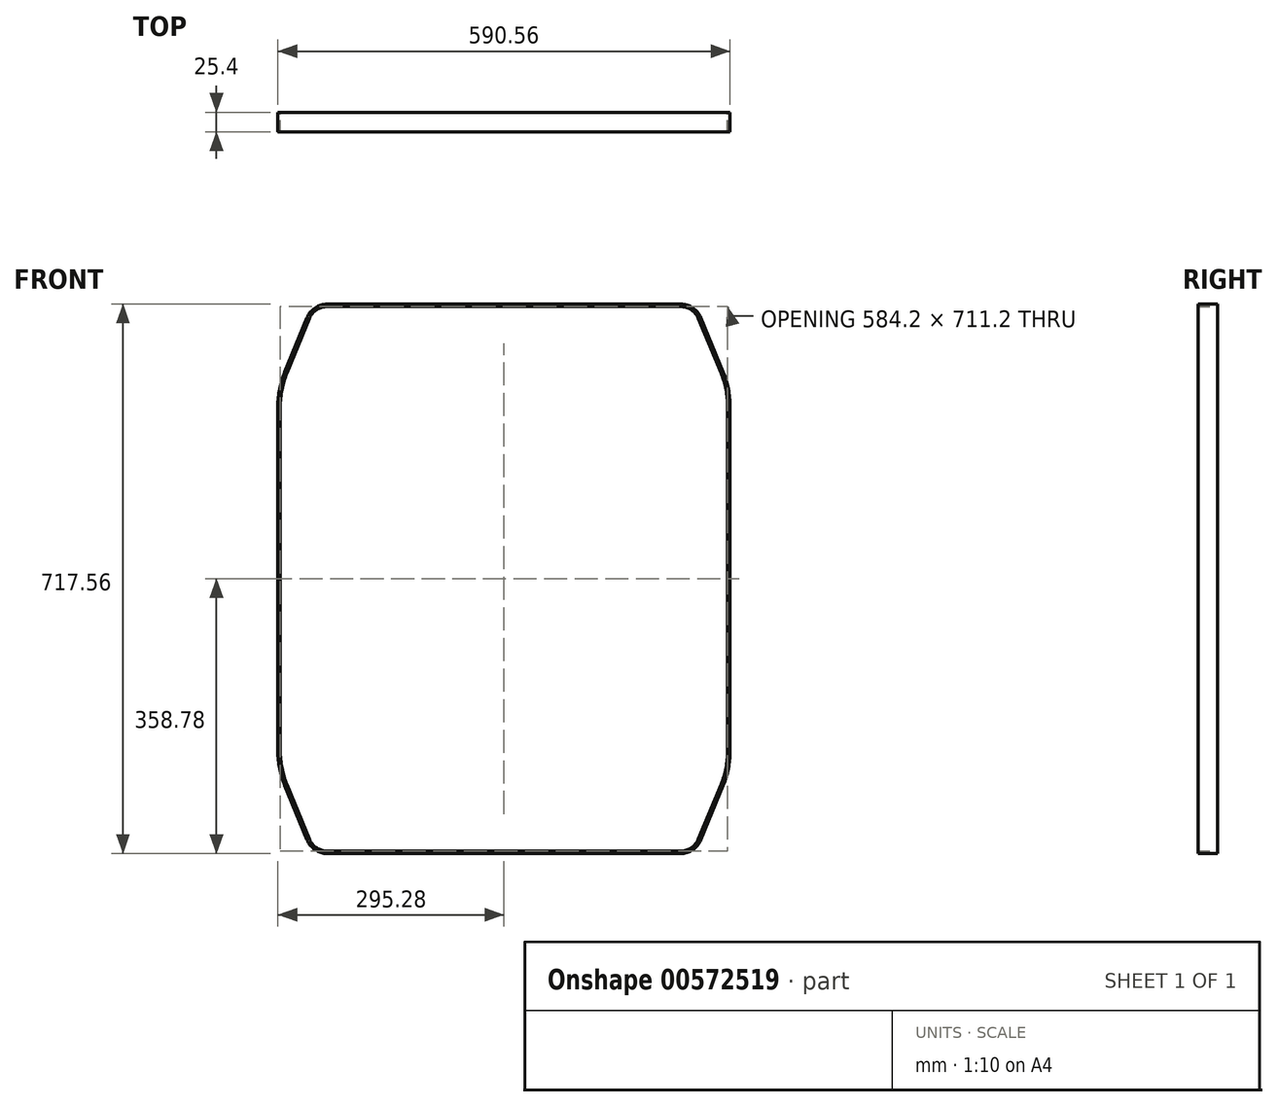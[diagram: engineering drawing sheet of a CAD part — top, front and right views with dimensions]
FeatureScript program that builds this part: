
annotation { "Feature Type Name" : "Feature", "Feature Type Description" : "" }
export const myFeature = defineFeature(function(context is Context, id is Id, definition is map)
    precondition{}
    {
        {
            var Q0;
            Q0=qCreatedBy(makeId("Front.planeOp"),FACE);
            var sketch = newSketch(context, id + "F0", { "sketchPlane" : qUnion([Q0])});
            skPoint(sketch, "E0", {"position": v(0, 0) * mm});
            skPoint(sketch, "E1", {"position": v(0, 711.2) * mm});
            skPoint(sketch, "E2", {"position": v(-584.2, 711.2) * mm});
            skPoint(sketch, "E3", {"position": v(-584.2, 0) * mm});
            skLineSegment(sketch, "E4", {"start": v(-514.35, 711.2) * mm, "end": v(-69.85, 711.2) * mm});
            skLineSegment(sketch, "E5", {"start": v(0, 577.85) * mm, "end": v(0, 133.35) * mm});
            skLineSegment(sketch, "E6", {"start": v(-69.85, 0) * mm, "end": v(-514.35, 0) * mm});
            skLineSegment(sketch, "E7", {"start": v(-584.2, 133.35) * mm, "end": v(-584.2, 577.85) * mm});
            skLineSegment(sketch, "E8", {"start": v(-514.35, 711.2) * mm, "end": v(-522.74, 711.2) * mm});
            skLineSegment(sketch, "E9", {"start": v(-546.23, 695.47) * mm, "end": v(-575.6, 624.16) * mm});
            skLineSegment(sketch, "E10", {"start": v(-584.2, 580.64) * mm, "end": v(-584.2, 577.85) * mm});
            skLineSegment(sketch, "E11", {"start": v(-69.85, 711.2) * mm, "end": v(-61.46, 711.2) * mm});
            skLineSegment(sketch, "E12", {"start": v(-37.97, 695.47) * mm, "end": v(-8.6, 624.16) * mm});
            skLineSegment(sketch, "E13", {"start": v(0, 580.64) * mm, "end": v(0, 577.85) * mm});
            skLineSegment(sketch, "E14", {"start": v(-514.35, 0) * mm, "end": v(-522.74, 0) * mm});
            skLineSegment(sketch, "E15", {"start": v(-546.23, 15.73) * mm, "end": v(-575.6, 87.04) * mm});
            skLineSegment(sketch, "E16", {"start": v(-584.2, 130.56) * mm, "end": v(-584.2, 133.35) * mm});
            skLineSegment(sketch, "E17", {"start": v(-69.85, 0) * mm, "end": v(-61.46, 0) * mm});
            skLineSegment(sketch, "E18", {"start": v(-37.97, 15.73) * mm, "end": v(-8.6, 87.04) * mm});
            skLineSegment(sketch, "E19", {"start": v(0, 130.56) * mm, "end": v(0, 133.35) * mm});
            skPoint(sketch, "E20.visualSharp", {"position": v(-539.75, 711.2) * mm});
            skArc(sketch, "E20.filletArc", {"start": v(-522.74, 711.2) * mm, "mid": v(-536.87, 706.9) * mm, "end": v(-546.23, 695.47) * mm});
            skPoint(sketch, "E21.visualSharp", {"position": v(-584.2, 603.25) * mm});
            skArc(sketch, "E21.filletArc", {"start": v(-575.6, 624.16) * mm, "mid": v(-582.03, 602.82) * mm, "end": v(-584.2, 580.64) * mm});
            skPoint(sketch, "E22.visualSharp", {"position": v(-584.2, 107.95) * mm});
            skArc(sketch, "E22.filletArc", {"start": v(-584.2, 130.56) * mm, "mid": v(-582.03, 108.38) * mm, "end": v(-575.6, 87.04) * mm});
            skPoint(sketch, "E23.visualSharp", {"position": v(-539.75, 0) * mm});
            skArc(sketch, "E23.filletArc", {"start": v(-546.23, 15.73) * mm, "mid": v(-536.87, 4.3) * mm, "end": v(-522.74, 0) * mm});
            skPoint(sketch, "E24.visualSharp", {"position": v(-44.45, 0) * mm});
            skArc(sketch, "E24.filletArc", {"start": v(-61.46, 0) * mm, "mid": v(-47.33, 4.3) * mm, "end": v(-37.97, 15.73) * mm});
            skPoint(sketch, "E25.visualSharp", {"position": v(0, 107.95) * mm});
            skArc(sketch, "E25.filletArc", {"start": v(-8.6, 87.04) * mm, "mid": v(-2.17, 108.38) * mm, "end": v(0, 130.56) * mm});
            skPoint(sketch, "E26.visualSharp", {"position": v(0, 603.25) * mm});
            skArc(sketch, "E26.filletArc", {"start": v(0, 580.64) * mm, "mid": v(-2.17, 602.82) * mm, "end": v(-8.6, 624.16) * mm});
            skPoint(sketch, "E27.visualSharp", {"position": v(-44.45, 711.2) * mm});
            skArc(sketch, "E27.filletArc", {"start": v(-37.97, 695.47) * mm, "mid": v(-47.33, 706.9) * mm, "end": v(-61.46, 711.2) * mm});
            skArc(sketch, "E28.0", {"start": v(-522.74, 714.38) * mm, "mid": v(-538.64, 709.54) * mm, "end": v(-549.16, 696.68) * mm});
            skLineSegment(sketch, "E28.1", {"start": v(-69.85, -3.17) * mm, "end": v(-61.46, -3.17) * mm});
            skLineSegment(sketch, "E28.2", {"start": v(-69.85, -3.17) * mm, "end": v(-514.35, -3.18) * mm});
            skLineSegment(sketch, "E28.3", {"start": v(-514.35, -3.18) * mm, "end": v(-522.74, -3.18) * mm});
            skArc(sketch, "E28.4", {"start": v(-549.16, 14.52) * mm, "mid": v(-538.64, 1.66) * mm, "end": v(-522.74, -3.18) * mm});
            skLineSegment(sketch, "E28.5", {"start": v(-549.16, 14.52) * mm, "end": v(-578.53, 85.83) * mm});
            skArc(sketch, "E28.6", {"start": v(-587.38, 130.56) * mm, "mid": v(-585.14, 107.76) * mm, "end": v(-578.53, 85.83) * mm});
            skArc(sketch, "E28.7", {"start": v(-578.53, 625.37) * mm, "mid": v(-585.14, 603.44) * mm, "end": v(-587.38, 580.64) * mm});
            skLineSegment(sketch, "E28.8", {"start": v(-587.38, 580.64) * mm, "end": v(-587.38, 577.85) * mm});
            skLineSegment(sketch, "E28.9", {"start": v(-587.38, 133.35) * mm, "end": v(-587.38, 577.85) * mm});
            skLineSegment(sketch, "E28.10", {"start": v(-587.38, 130.56) * mm, "end": v(-587.38, 133.35) * mm});
            skArc(sketch, "E28.11", {"start": v(-61.46, -3.17) * mm, "mid": v(-45.56, 1.66) * mm, "end": v(-35.04, 14.52) * mm});
            skLineSegment(sketch, "E28.12", {"start": v(-549.16, 696.68) * mm, "end": v(-578.53, 625.37) * mm});
            skLineSegment(sketch, "E28.13", {"start": v(-35.04, 14.52) * mm, "end": v(-5.67, 85.83) * mm});
            skArc(sketch, "E28.14", {"start": v(-5.67, 85.83) * mm, "mid": v(0.94, 107.76) * mm, "end": v(3.18, 130.56) * mm});
            skLineSegment(sketch, "E28.15", {"start": v(3.18, 130.56) * mm, "end": v(3.18, 133.35) * mm});
            skLineSegment(sketch, "E28.16", {"start": v(3.18, 577.85) * mm, "end": v(3.18, 133.35) * mm});
            skLineSegment(sketch, "E28.17", {"start": v(3.18, 580.64) * mm, "end": v(3.18, 577.85) * mm});
            skArc(sketch, "E28.18", {"start": v(3.18, 580.64) * mm, "mid": v(0.94, 603.44) * mm, "end": v(-5.67, 625.37) * mm});
            skLineSegment(sketch, "E28.19", {"start": v(-35.04, 696.68) * mm, "end": v(-5.67, 625.37) * mm});
            skArc(sketch, "E28.20", {"start": v(-35.04, 696.68) * mm, "mid": v(-45.56, 709.54) * mm, "end": v(-61.46, 714.38) * mm});
            skLineSegment(sketch, "E28.21", {"start": v(-69.85, 714.38) * mm, "end": v(-61.46, 714.38) * mm});
            skLineSegment(sketch, "E28.22", {"start": v(-514.35, 714.38) * mm, "end": v(-69.85, 714.38) * mm});
            skLineSegment(sketch, "E28.23", {"start": v(-514.35, 714.38) * mm, "end": v(-522.74, 714.38) * mm});
            skSolve(sketch);
        }
        {
            var Q0;
            Q0 = qSketchRegion(id + "F0", true);
            extrude(context, id + "F1", {"entities" : qUnion([Q0]), "depth" : 25.4 * mm, "offsetDistance" : 25.4 * mm});
        }
    });
